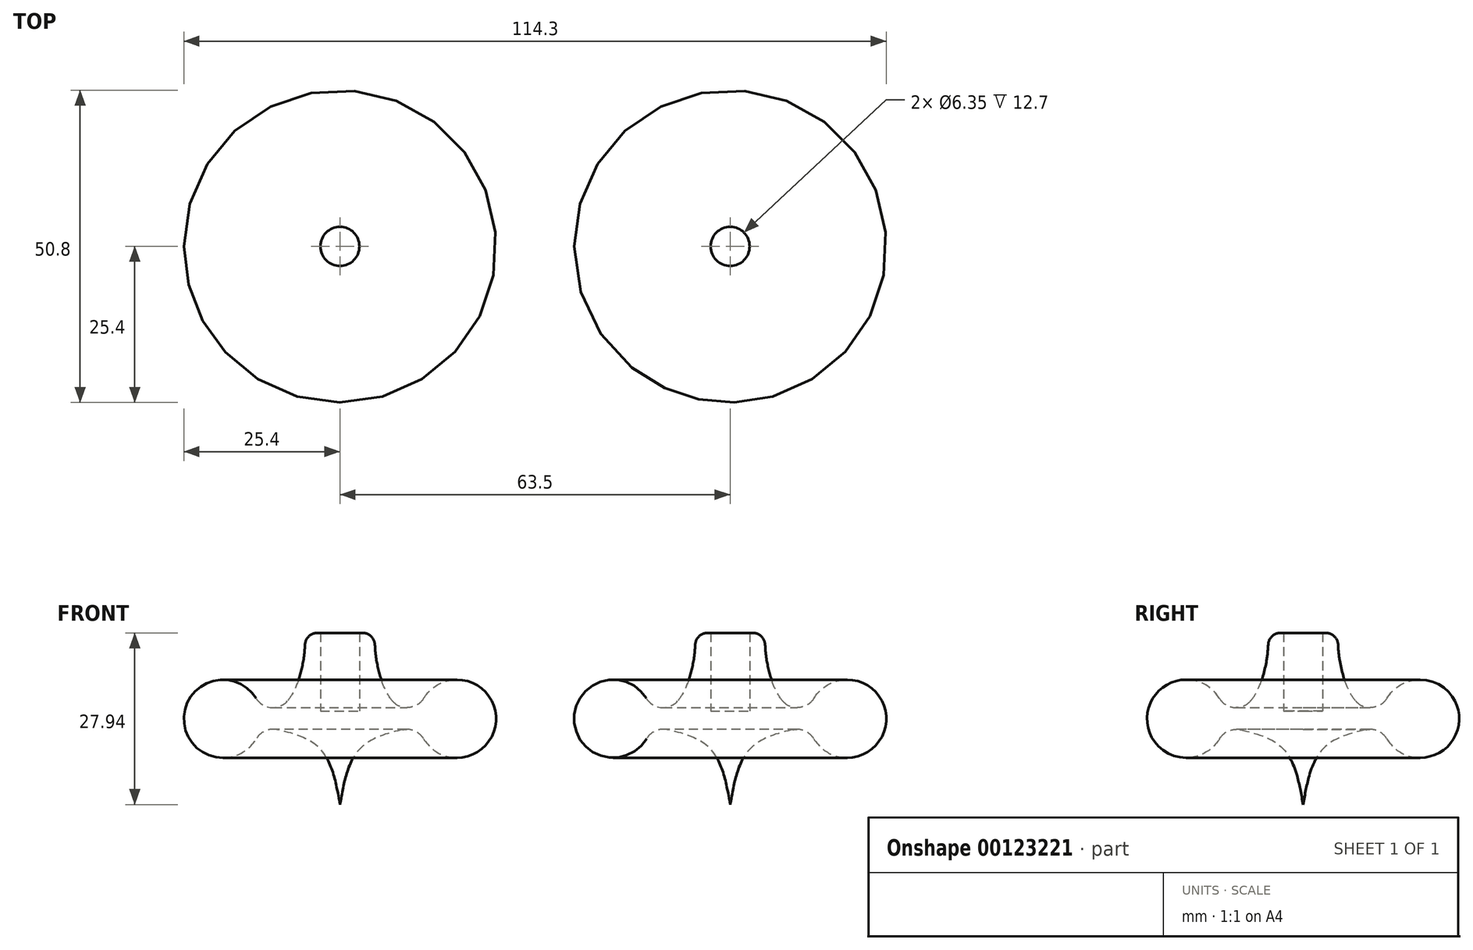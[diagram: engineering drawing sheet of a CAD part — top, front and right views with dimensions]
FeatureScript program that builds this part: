
annotation { "Feature Type Name" : "Feature", "Feature Type Description" : "" }
export const myFeature = defineFeature(function(context is Context, id is Id, definition is map)
    precondition{}
    {
        {
            var Q0;
            Q0=qCreatedBy(makeId("Front.planeOp"),FACE);
            var sketch = newSketch(context, id + "F0", { "sketchPlane" : qUnion([Q0])});
            skLineSegment(sketch, "E0", {"start": v(0, -27.94) * mm, "end": v(0, -12.7) * mm});
            skLineSegment(sketch, "E1.top", {"start": v(0, -12.7) * mm, "end": v(-3.17, -12.7) * mm});
            skLineSegment(sketch, "E1.right", {"start": v(-3.18, 0) * mm, "end": v(-3.18, -12.7) * mm});
            skPoint(sketch, "E2.visualSharp", {"position": v(-5.72, 0) * mm});
            skLineSegment(sketch, "E3", {"start": v(-3.18, 0) * mm, "end": v(-3.66, 0) * mm});
            skArc(sketch, "E4", {"start": v(-13.64, -10.65) * mm, "mid": v(-25.4, -14) * mm, "end": v(-13.6, -17.23) * mm});
            skLineSegment(sketch, "E5", {"start": v(-10.41, -15.24) * mm, "end": v(-15.24, -15.24) * mm, "construction": true});
            skLineSegment(sketch, "E6", {"start": v(-10.67, -12.7) * mm, "end": v(-14.99, -12.7) * mm, "construction": true});
            skFitSpline(sketch, "E7", {"points": [v(-5.72, 0) * mm, v(-8.42, -10.95) * mm, v(-12.83, -12.7) * mm], "startDerivative": vector(1.45, -21.17) * mm, "endDerivative": vector(-16.39, -1.82) * mm});
            skFitSpline(sketch, "E8", {"points": [v(0, -27.94) * mm, v(-3.36, -18.76) * mm, v(-12.83, -15.24) * mm], "startDerivative": vector(-3.81, 21.28) * mm, "endDerivative": vector(-21.45, 4.14) * mm});
            skArc(sketch, "E9.filletArc", {"start": v(-13.64, -10.65) * mm, "mid": v(-11.2, -12.16) * mm, "end": v(-8.54, -11.08) * mm});
            skArc(sketch, "E10.filletArc", {"start": v(-10.2, -15.76) * mm, "mid": v(-12.14, -15.95) * mm, "end": v(-13.6, -17.23) * mm});
            skArc(sketch, "E11.filletArc", {"start": v(-3.66, 0) * mm, "mid": v(-5.07, -0.57) * mm, "end": v(-5.7, -1.95) * mm});
            skSolve(sketch);
        }
        {
            var Q0;
            Q0=makeQuery(id+"F0.imprint","IMPRINT",FACE,{"disambiguationData":[TD([[makeQuery(id+"F0.imprint","IMPRINT",EDGE,{"derivedFrom":sQuery(id+"F0.wireOp",EDGE,"E0")}),1.0]])]});
            var Q1;
            Q1=sQuery(id+"F0.wireOp",EDGE,"E0");
            revolve(context, id + "F1", {"entities" : qUnion([Q0]), "axis" : qUnion([Q1]), "revolveType" : RevolveType.FULL});
        }
        {
            var Q0;
            Q0=makeQuery(id+"F1.opRevolve","SWEPT_BODY",BODY,{"disambiguationData":[OSD([sQuery(id+"F0.wireOp",EDGE,"E0"),sQuery(id+"F0.wireOp",EDGE,"E1.top"),sQuery(id+"F0.wireOp",EDGE,"E1.right"),sQuery(id+"F0.wireOp",EDGE,"E3"),sQuery(id+"F0.wireOp",EDGE,"E4"),sQuery(id+"F0.wireOp",EDGE,"E7"),sQuery(id+"F0.wireOp",EDGE,"E8"),sQuery(id+"F0.wireOp",EDGE,"E9.filletArc"),sQuery(id+"F0.wireOp",EDGE,"E10.filletArc"),sQuery(id+"F0.wireOp",EDGE,"E11.filletArc")])]});
            transform(context, id + "F2", {"entities" : qUnion([Q0]), "transformType" : TransformType.TRANSLATION_3D, "dx" : 63.5 * mm, "dy" : 0 * mm, "dz" : 0 * mm, "makeCopy" : true});
        }
    });
